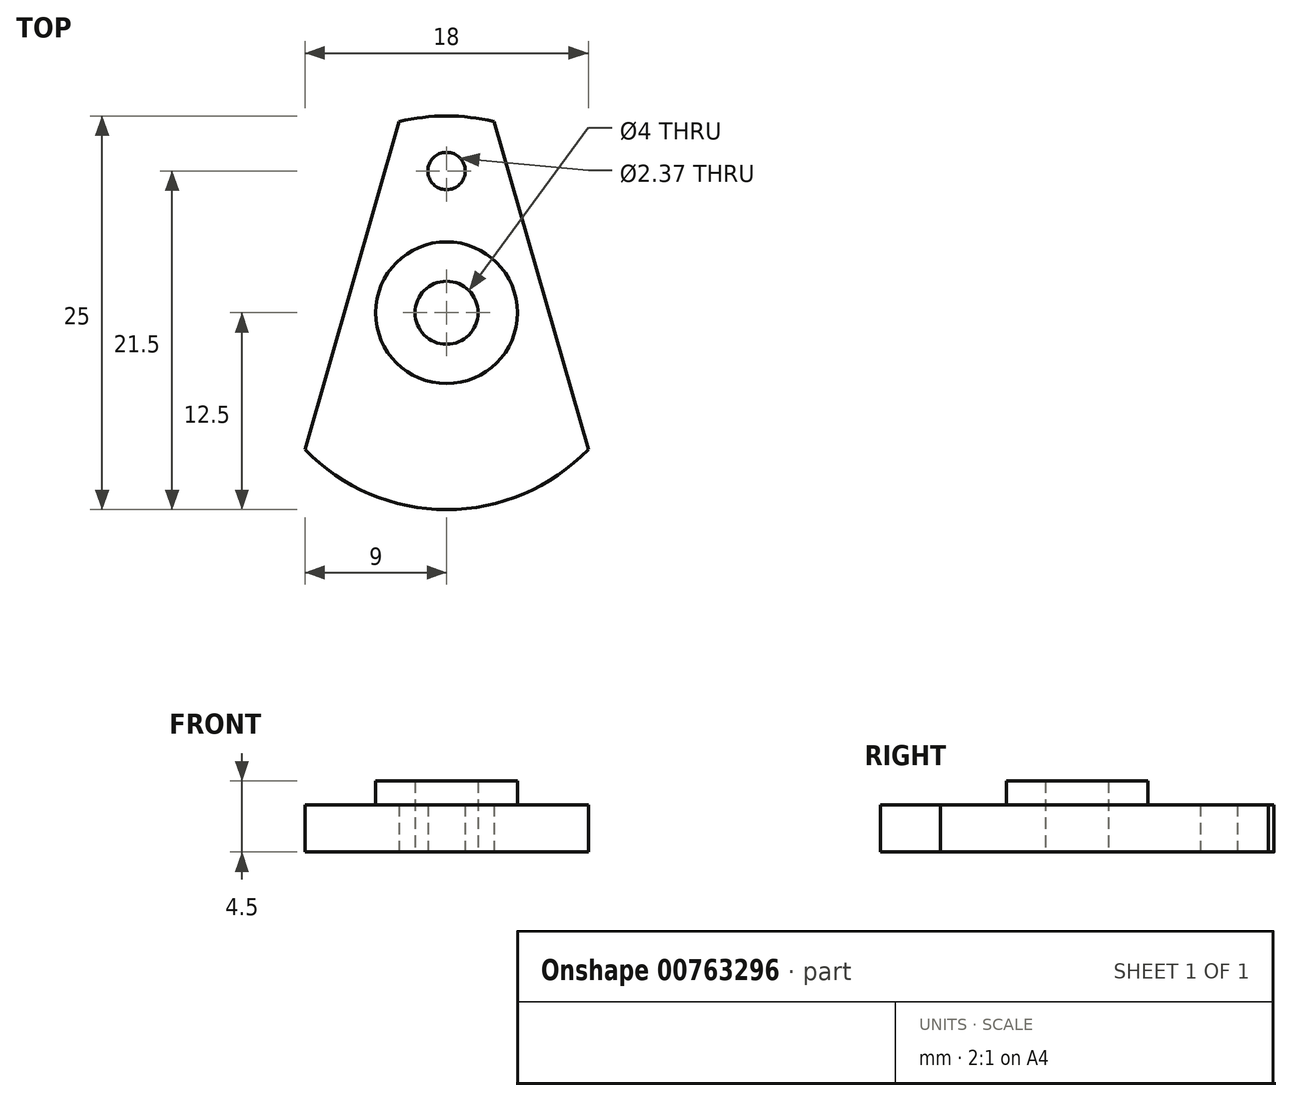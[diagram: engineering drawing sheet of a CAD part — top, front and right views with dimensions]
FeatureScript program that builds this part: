
annotation { "Feature Type Name" : "Feature", "Feature Type Description" : "" }
export const myFeature = defineFeature(function(context is Context, id is Id, definition is map)
    precondition{}
    {
        {
            var Q0;
            Q0=qCreatedBy(makeId("Top.planeOp"),FACE);
            var sketch = newSketch(context, id + "F0", { "sketchPlane" : qUnion([Q0])});
            skArc(sketch, "E0", {"start": v(-9, -8.67) * mm, "mid": v(0, -12.5) * mm, "end": v(9, -8.67) * mm});
            skLineSegment(sketch, "E1", {"start": v(3, 12.13) * mm, "end": v(9, -8.67) * mm});
            skLineSegment(sketch, "E2.MirrorCS", {"start": v(-3, 12.13) * mm, "end": v(-9, -8.67) * mm});
            skArc(sketch, "E3.trimOffspring", {"start": v(3, 12.13) * mm, "mid": v(0, 12.5) * mm, "end": v(-3, 12.13) * mm});
            skCircle(sketch, "E4", {"center": v(0, 0) * mm, "radius": 4.5 * mm});
            skCircle(sketch, "E5", {"center": v(0, 0) * mm, "radius": 2 * mm});
            skCircle(sketch, "E6", {"center": v(0, 9) * mm, "radius": 1.19 * mm});
            skSolve(sketch);
        }
        {
            var Q0;
            Q0=makeQuery(id+"F0.imprint","IMPRINT",FACE,{"disambiguationData":[TD([[makeQuery(id+"F0.imprint","IMPRINT",EDGE,{"derivedFrom":sQuery(id+"F0.wireOp",EDGE,"E4")}),1.0]])]});
            extrude(context, id + "F1", {"entities" : qUnion([Q0]), "depth" : 4.5 * mm, "offsetDistance" : 25 * mm});
        }
        {
            var Q0;
            Q0=makeQuery(id+"F0.imprint","IMPRINT",FACE,{"disambiguationData":[TD([[makeQuery(id+"F0.imprint","IMPRINT",EDGE,{"derivedFrom":sQuery(id+"F0.wireOp",EDGE,"E0")}),1.0]])]});
            extrude(context, id + "F2", {"entities" : qUnion([Q0]), "operationType" : NewBodyOperationType.ADD, "depth" : 3 * mm, "offsetDistance" : 25 * mm});
        }
    });
